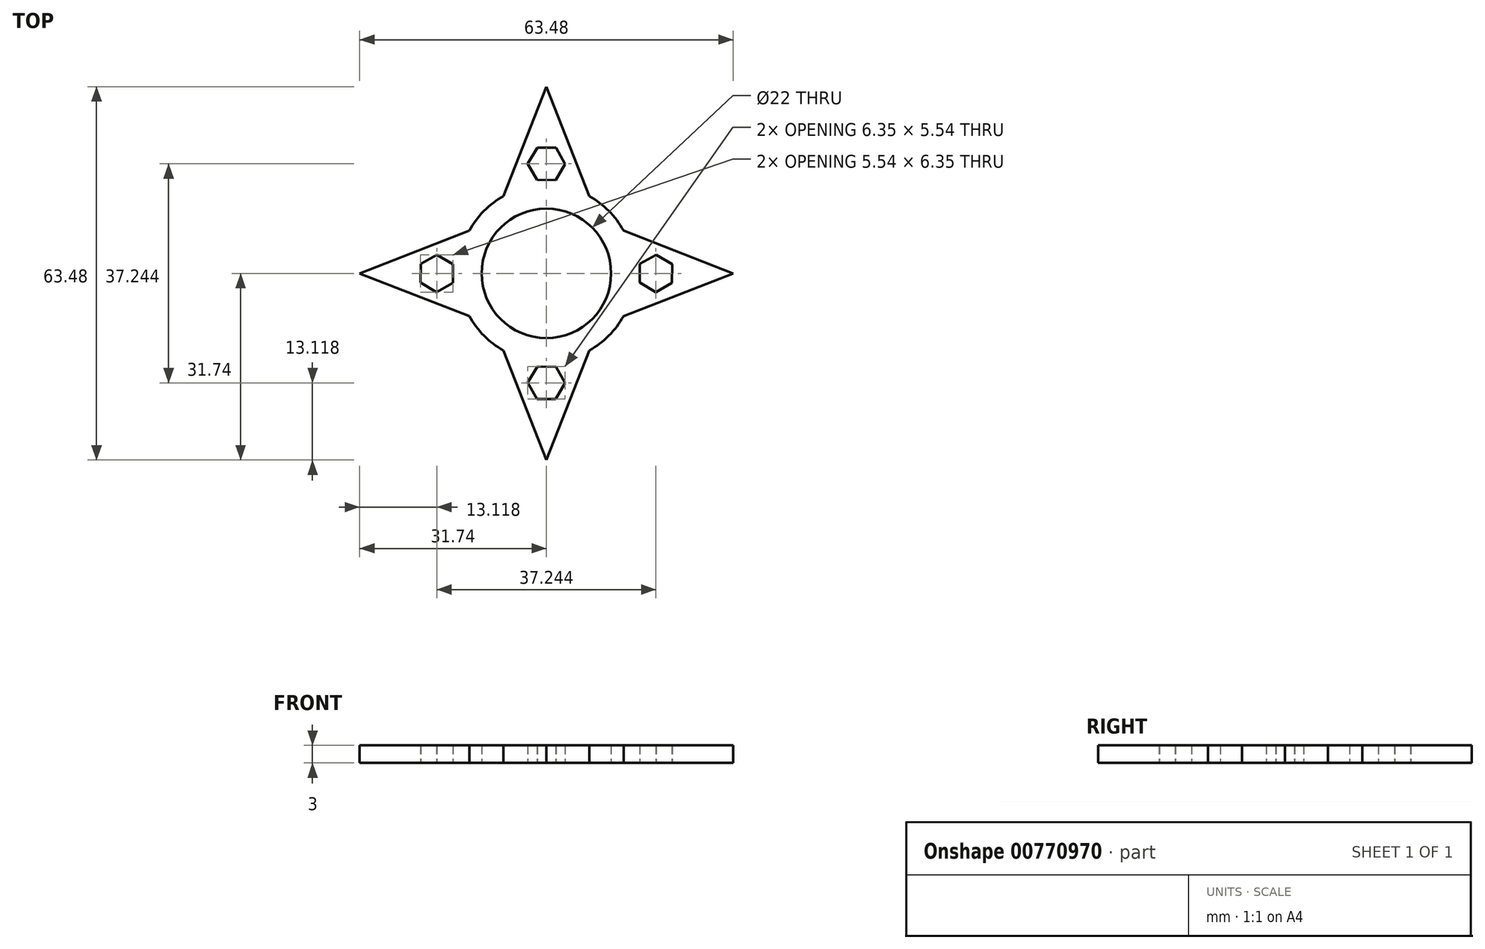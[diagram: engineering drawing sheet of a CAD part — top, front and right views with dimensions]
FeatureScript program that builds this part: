
annotation { "Feature Type Name" : "Feature", "Feature Type Description" : "" }
export const myFeature = defineFeature(function(context is Context, id is Id, definition is map)
    precondition{}
    {
        {
            var Q0;
            Q0=qCreatedBy(makeId("Top.planeOp"),FACE);
            var sketch = newSketch(context, id + "F0", { "sketchPlane" : qUnion([Q0])});
            skLineSegment(sketch, "E0", {"start": v(-40.73, 0) * mm, "end": v(15, 0) * mm});
            skArc(sketch, "E1", {"start": v(11, 0) * mm, "mid": v(0, 11) * mm, "end": v(-11, 0) * mm});
            skArc(sketch, "E2", {"start": v(15, 0) * mm, "mid": v(0, 15) * mm, "end": v(-15, 0) * mm});
            skLineSegment(sketch, "E3", {"start": v(-7.28, 13.12) * mm, "end": v(0, 31.74) * mm});
            skLineSegment(sketch, "E4", {"start": v(0, 31.74) * mm, "end": v(7.28, 13.12) * mm});
            skCircle(sketch, "E5.cCircle", {"center": v(0, 18.62) * mm, "radius": 2.75 * mm, "construction": true});
            skLineSegment(sketch, "E5.0", {"start": v(-3.18, 18.66) * mm, "end": v(-1.56, 21.4) * mm});
            skLineSegment(sketch, "E5.1", {"start": v(-1.56, 21.4) * mm, "end": v(1.62, 21.35) * mm});
            skLineSegment(sketch, "E5.2", {"start": v(1.62, 21.35) * mm, "end": v(3.18, 18.59) * mm});
            skLineSegment(sketch, "E5.3", {"start": v(3.18, 18.59) * mm, "end": v(1.56, 15.85) * mm});
            skLineSegment(sketch, "E5.4", {"start": v(1.56, 15.85) * mm, "end": v(-1.62, 15.9) * mm});
            skLineSegment(sketch, "E5.5", {"start": v(-1.62, 15.9) * mm, "end": v(-3.18, 18.66) * mm});
            skPoint(sketch, "E5.0.midPoint", {"position": v(-2.37, 20.02) * mm});
            skLineSegment(sketch, "E6", {"start": v(-11, 0) * mm, "end": v(0, 0) * mm});
            skLineSegment(sketch, "E7.trimOffspring", {"start": v(11, 0) * mm, "end": v(15, 0) * mm});
            skLineSegment(sketch, "E8.1.0", {"start": v(-31.74, 0) * mm, "end": v(-13.12, 7.28) * mm});
            skLineSegment(sketch, "E8.1.1", {"start": v(-13.12, -7.28) * mm, "end": v(-31.74, 0) * mm});
            skLineSegment(sketch, "E8.1.2", {"start": v(-21.35, 1.62) * mm, "end": v(-18.59, 3.18) * mm});
            skLineSegment(sketch, "E8.1.3", {"start": v(-18.59, 3.18) * mm, "end": v(-15.85, 1.56) * mm});
            skLineSegment(sketch, "E8.1.4", {"start": v(-15.85, 1.56) * mm, "end": v(-15.9, -1.62) * mm});
            skLineSegment(sketch, "E8.1.5", {"start": v(-15.9, -1.62) * mm, "end": v(-18.66, -3.18) * mm});
            skLineSegment(sketch, "E8.1.6", {"start": v(-18.66, -3.18) * mm, "end": v(-21.4, -1.56) * mm});
            skLineSegment(sketch, "E8.1.7", {"start": v(-21.4, -1.56) * mm, "end": v(-21.35, 1.62) * mm});
            skArc(sketch, "E8.1.8", {"start": v(0, 15) * mm, "mid": v(-15, 0) * mm, "end": v(0, -15) * mm});
            skArc(sketch, "E8.1.9", {"start": v(0, 11) * mm, "mid": v(-11, 0) * mm, "end": v(0, -11) * mm});
            skLineSegment(sketch, "E8.2.0", {"start": v(0, -31.74) * mm, "end": v(-7.28, -13.12) * mm});
            skLineSegment(sketch, "E8.2.1", {"start": v(7.28, -13.12) * mm, "end": v(0, -31.74) * mm});
            skLineSegment(sketch, "E8.2.2", {"start": v(-1.62, -21.35) * mm, "end": v(-3.18, -18.59) * mm});
            skLineSegment(sketch, "E8.2.3", {"start": v(-3.18, -18.59) * mm, "end": v(-1.56, -15.85) * mm});
            skLineSegment(sketch, "E8.2.4", {"start": v(-1.56, -15.85) * mm, "end": v(1.62, -15.9) * mm});
            skLineSegment(sketch, "E8.2.5", {"start": v(1.62, -15.9) * mm, "end": v(3.18, -18.66) * mm});
            skLineSegment(sketch, "E8.2.6", {"start": v(3.18, -18.66) * mm, "end": v(1.56, -21.4) * mm});
            skLineSegment(sketch, "E8.2.7", {"start": v(1.56, -21.4) * mm, "end": v(-1.62, -21.35) * mm});
            skArc(sketch, "E8.2.8", {"start": v(-15, 0) * mm, "mid": v(0, -15) * mm, "end": v(15, 0) * mm});
            skArc(sketch, "E8.2.9", {"start": v(-11, 0) * mm, "mid": v(0, -11) * mm, "end": v(11, 0) * mm});
            skLineSegment(sketch, "E8.3.0", {"start": v(31.74, 0) * mm, "end": v(13.12, -7.28) * mm});
            skLineSegment(sketch, "E8.3.1", {"start": v(13.12, 7.28) * mm, "end": v(31.74, 0) * mm});
            skLineSegment(sketch, "E8.3.2", {"start": v(21.35, -1.62) * mm, "end": v(18.59, -3.18) * mm});
            skLineSegment(sketch, "E8.3.3", {"start": v(18.59, -3.18) * mm, "end": v(15.85, -1.56) * mm});
            skLineSegment(sketch, "E8.3.4", {"start": v(15.85, -1.56) * mm, "end": v(15.9, 1.62) * mm});
            skLineSegment(sketch, "E8.3.5", {"start": v(15.9, 1.62) * mm, "end": v(18.66, 3.18) * mm});
            skLineSegment(sketch, "E8.3.6", {"start": v(18.66, 3.18) * mm, "end": v(21.4, 1.56) * mm});
            skLineSegment(sketch, "E8.3.7", {"start": v(21.4, 1.56) * mm, "end": v(21.35, -1.62) * mm});
            skArc(sketch, "E8.3.8", {"start": v(0, -15) * mm, "mid": v(15, 0) * mm, "end": v(0, 15) * mm});
            skArc(sketch, "E8.3.9", {"start": v(0, -11) * mm, "mid": v(11, 0) * mm, "end": v(0, 11) * mm});
            skSolve(sketch);
        }
        {
            var Q0;
            Q0 = qSketchRegion(id + "F0", true);
            extrude(context, id + "F1", {"entities" : qUnion([Q0]), "depth" : 3 * mm, "offsetDistance" : 25 * mm});
        }
    });
